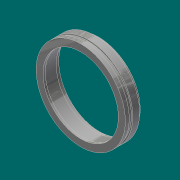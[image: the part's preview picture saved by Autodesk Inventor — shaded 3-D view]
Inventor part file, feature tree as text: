
AUTODESK INVENTOR PART (.ipt)
format: ipt  version: 2017.3 (Build 213257000, 257)  size: 220,160 bytes
history: native  units: in
note: dims shown in document units (in); Inventor stores cm internally (conversion verified against a paired STEP export)
features: revolve x1, chamfer x1, sketch x1
ambient origin geometry x8: Origin, YZ Plane, XZ Plane, XY Plane, X Axis, Y Axis, Z Axis, Center Point
bodies: Solid1 (feature_tree)
feature tree (3):
  revolve  "Revolution1"  [1 undecoded]
  chamfer  "Chamfer2"  Angle=90.0deg  [1 undecoded]
  sketch  "Sketch1"  dims[d0=16.25in d5=1.0in d6=90.0deg d13=18.75in d14=19.25in d16=1.75in d17=1.35in d18=0.0515in d19=0.0842in d20=0.0312in d21=0.125in d22=45.0deg d32=18.0in d33=0.4375in d35=0.0625in d36=0.25in d38=8.0in d44=0.5in d46=0.2577in d47=0.5in d48=16.75in d49=6.1875in]
note: 2 required parameter values undecoded (feature->parameter linkage not recoverable at this tier; creation-order binding heuristic only, values carry confidence <= 0.55)